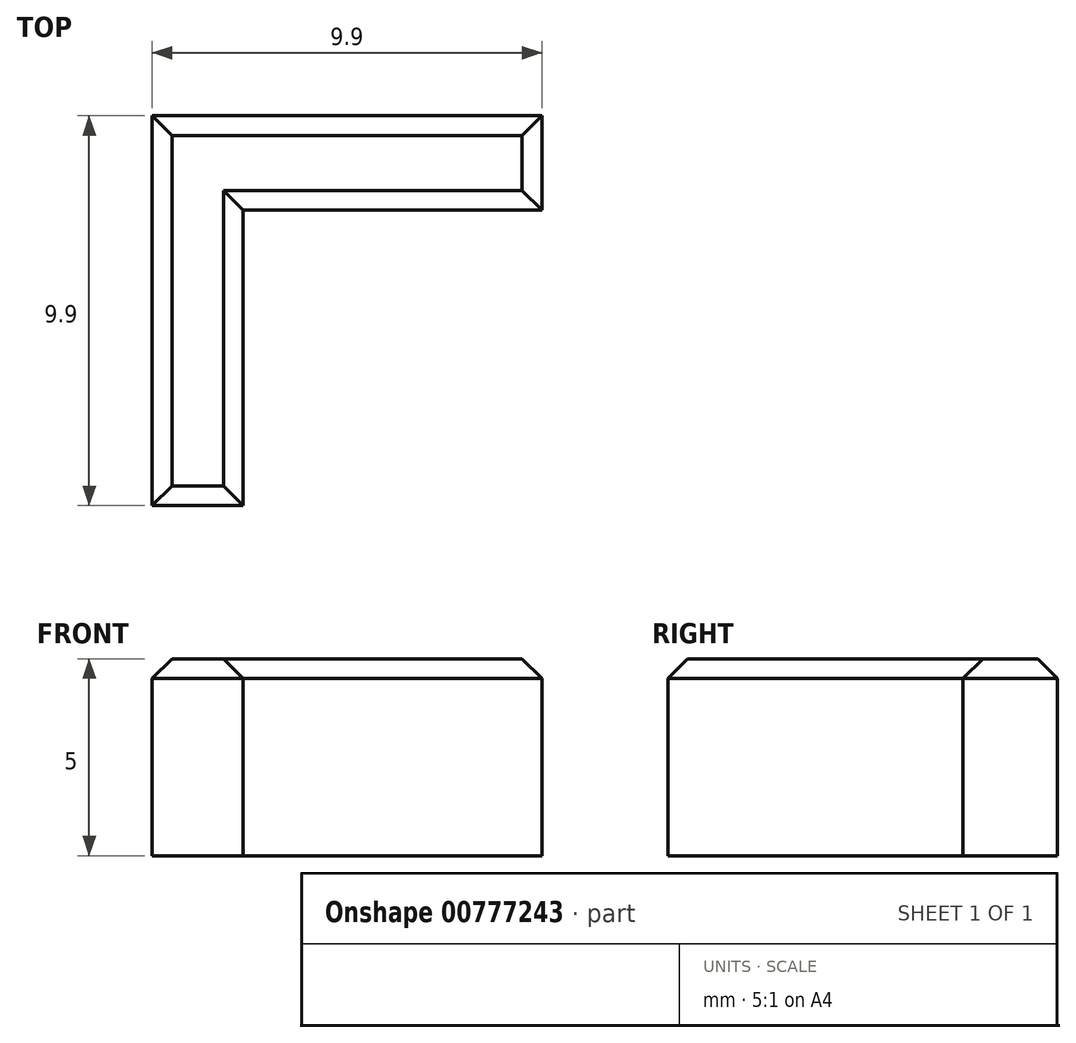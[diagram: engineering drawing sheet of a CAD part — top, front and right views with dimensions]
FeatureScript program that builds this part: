
annotation { "Feature Type Name" : "Feature", "Feature Type Description" : "" }
export const myFeature = defineFeature(function(context is Context, id is Id, definition is map)
    precondition{}
    {
        {
            var Q0;
            Q0=qCreatedBy(makeId("Top.planeOp"),FACE);
            var sketch = newSketch(context, id + "F0", { "sketchPlane" : qUnion([Q0])});
            skLineSegment(sketch, "E0.bottom", {"start": v(-2.36, 2.4) * mm, "end": v(7.54, 2.4) * mm});
            skLineSegment(sketch, "E0.top", {"start": v(-2.36, -7.5) * mm, "end": v(-0.05, -7.5) * mm});
            skLineSegment(sketch, "E0.left", {"start": v(-2.36, 2.4) * mm, "end": v(-2.36, -7.5) * mm});
            skLineSegment(sketch, "E0.right", {"start": v(7.54, 2.4) * mm, "end": v(7.54, 0) * mm});
            skLineSegment(sketch, "E1.bottom", {"start": v(-0.05, 0) * mm, "end": v(7.54, 0) * mm});
            skLineSegment(sketch, "E1.left", {"start": v(-0.05, 0) * mm, "end": v(-0.05, -7.5) * mm});
            skSolve(sketch);
        }
        {
            var Q0;
            Q0 = qSketchRegion(id + "F0", true);
            extrude(context, id + "F1", {"entities" : qUnion([Q0]), "depth" : 5 * mm, "offsetDistance" : 25 * mm});
        }
        {
            var Q0;
            Q0=makeQuery(id+"F1.opExtrude","CAP_FACE",FACE,{"disambiguationData":[OSD([sQuery(id+"F0.wireOp",EDGE,"E0.bottom"),sQuery(id+"F0.wireOp",EDGE,"E0.top"),sQuery(id+"F0.wireOp",EDGE,"E0.left"),sQuery(id+"F0.wireOp",EDGE,"E0.right"),sQuery(id+"F0.wireOp",EDGE,"E1.bottom"),sQuery(id+"F0.wireOp",EDGE,"E1.left")])],"isStart":false});
            chamfer(context, id + "F2", {"entities" : qUnion([Q0]), "width" : 0.5 * mm, "tangentPropagation" : true});
        }
    });
